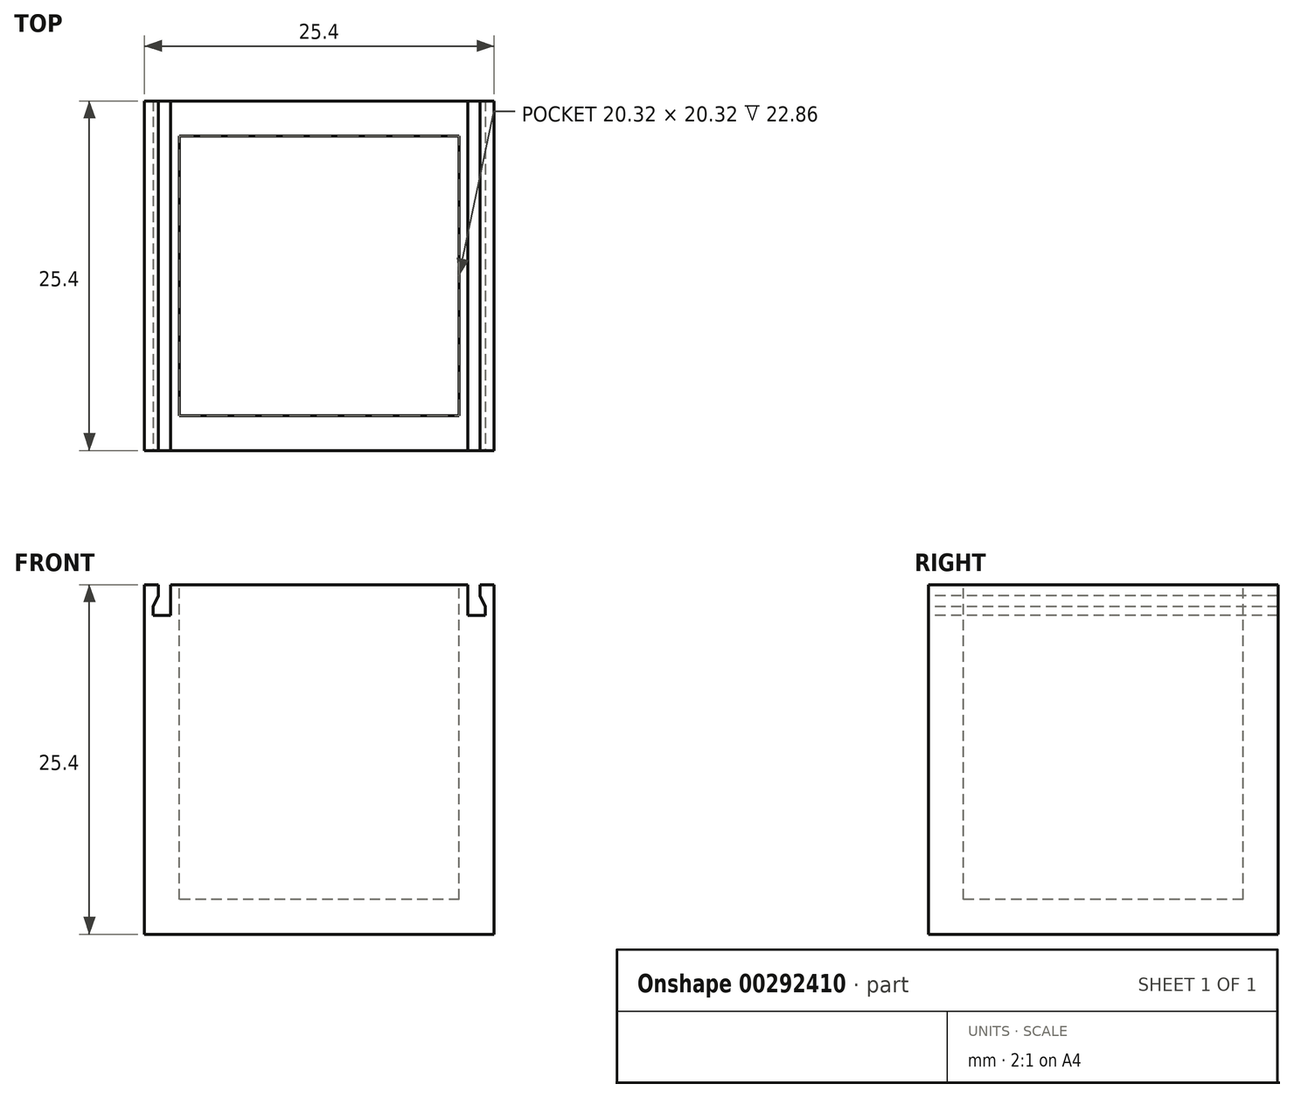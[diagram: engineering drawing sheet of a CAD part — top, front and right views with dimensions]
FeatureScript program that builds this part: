
annotation { "Feature Type Name" : "Feature", "Feature Type Description" : "" }
export const myFeature = defineFeature(function(context is Context, id is Id, definition is map)
    precondition{}
    {
        {
            var Q0;
            Q0=qCreatedBy(makeId("Front.planeOp"),FACE);
            var sketch = newSketch(context, id + "F0", { "sketchPlane" : qUnion([Q0])});
            skLineSegment(sketch, "E0.bottom", {"start": v(12.7, -12.7) * mm, "end": v(-12.7, -12.7) * mm});
            skLineSegment(sketch, "E0.top", {"start": v(12.7, 12.7) * mm, "end": v(-12.7, 12.7) * mm});
            skLineSegment(sketch, "E0.left", {"start": v(12.7, -12.7) * mm, "end": v(12.7, 12.7) * mm});
            skLineSegment(sketch, "E0.right", {"start": v(-12.7, -12.7) * mm, "end": v(-12.7, 12.7) * mm});
            skPoint(sketch, "E0.middle", {"position": v(0, 0) * mm});
            skLineSegment(sketch, "E1", {"start": v(0, 0) * mm, "end": v(0, 12.7) * mm});
            skLineSegment(sketch, "E2", {"start": v(-12.7, 12.7) * mm, "end": v(0, 12.7) * mm});
            skSolve(sketch);
        }
        {
            var Q0;
            Q0=qCreatedBy(makeId("Top.planeOp"),FACE);
            var sketch = newSketch(context, id + "F1", { "sketchPlane" : qUnion([Q0])});
            skLineSegment(sketch, "E3", {"start": v(0, 0) * mm, "end": v(0, 12.7) * mm});
            skLineSegment(sketch, "E4.bottom", {"start": v(11.43, 1.27) * mm, "end": v(-11.43, 1.27) * mm});
            skLineSegment(sketch, "E4.top", {"start": v(11.43, 24.13) * mm, "end": v(-11.43, 24.13) * mm});
            skLineSegment(sketch, "E4.left", {"start": v(11.43, 1.27) * mm, "end": v(11.43, 24.13) * mm});
            skLineSegment(sketch, "E4.right", {"start": v(-11.43, 1.27) * mm, "end": v(-11.43, 24.13) * mm});
            skPoint(sketch, "E4.middle", {"position": v(0, 12.7) * mm});
            skSolve(sketch);
        }
        {
            var Q0;
            Q0=makeQuery(id+"F1.imprint","IMPRINT",FACE,{"disambiguationData":[TD([[makeQuery(id+"F1.imprint","IMPRINT",EDGE,{"derivedFrom":sQuery(id+"F1.wireOp",EDGE,"E4.top")}),1.0]])]});
            extrude(context, id + "F2", {"entities" : qUnion([Q0]), "endBound" : BoundingType.SYMMETRIC, "depth" : 22.86 * mm});
        }
        {
            var Q0;
            Q0 = qSketchRegion(id + "F0", true);
            extrude(context, id + "F3", {"entities" : qUnion([Q0]), "oppositeDirection" : true, "depth" : 25.4 * mm});
        }
        {
            var Q0;
            Q0=makeQuery(id+"F3.opExtrude","SWEPT_FACE",FACE,{"disambiguationData":[OSD([sQuery(id+"F0.wireOp",EDGE,"E0.top"),sQuery(id+"F0.wireOp",EDGE,"E2")])]});
            shell(context, id + "F4", {"entities" : qUnion([Q0]), "thickness" : 2.54 * mm});
        }
        {
            var Q0;
            Q0=makeQuery(id+"F2.opExtrude","SWEPT_BODY",BODY,{"disambiguationData":[OSD([sQuery(id+"F1.wireOp",EDGE,"E4.bottom"),sQuery(id+"F1.wireOp",EDGE,"E4.top"),sQuery(id+"F1.wireOp",EDGE,"E4.left"),sQuery(id+"F1.wireOp",EDGE,"E4.right")])]});
            deleteBodies(context, id + "F5", {"entities" : qUnion([Q0])});
        }
        {
            var Q0;
            Q0=qCreatedBy(makeId("Front.planeOp"),FACE);
            var sketch = newSketch(context, id + "F6", { "sketchPlane" : qUnion([Q0])});
            skLineSegment(sketch, "E5.bottom", {"start": v(-10.8, 10.48) * mm, "end": v(-12.06, 10.48) * mm});
            skLineSegment(sketch, "E5.left", {"start": v(-10.8, 10.48) * mm, "end": v(-10.8, 11.11) * mm});
            skLineSegment(sketch, "E5.right", {"start": v(-12.06, 10.48) * mm, "end": v(-12.06, 11.11) * mm});
            skLineSegment(sketch, "E6.bottom", {"start": v(12.07, 10.48) * mm, "end": v(10.8, 10.48) * mm});
            skLineSegment(sketch, "E6.left", {"start": v(12.07, 10.48) * mm, "end": v(12.07, 11.11) * mm});
            skLineSegment(sketch, "E6.right", {"start": v(10.8, 10.48) * mm, "end": v(10.8, 11.11) * mm});
            skLineSegment(sketch, "E7.0", {"start": v(-11.68, 12.7) * mm, "end": v(-11.68, 11.9) * mm});
            skLineSegment(sketch, "E8.0", {"start": v(11.68, 12.7) * mm, "end": v(11.68, 11.9) * mm});
            skLineSegment(sketch, "E9", {"start": v(11.68, 11.9) * mm, "end": v(12.07, 11.11) * mm});
            skLineSegment(sketch, "E10", {"start": v(-12.06, 11.11) * mm, "end": v(-11.68, 11.9) * mm});
            skLineSegment(sketch, "E11", {"start": v(-10.8, 11.11) * mm, "end": v(-10.8, 12.7) * mm});
            skLineSegment(sketch, "E12", {"start": v(-11.68, 12.7) * mm, "end": v(-10.8, 12.7) * mm});
            skLineSegment(sketch, "E13", {"start": v(10.8, 11.11) * mm, "end": v(10.8, 12.7) * mm});
            skLineSegment(sketch, "E14", {"start": v(10.8, 12.7) * mm, "end": v(11.68, 12.7) * mm});
            skSolve(sketch);
        }
        {
            var Q0;
            Q0=makeQuery(id+"F6.imprint","IMPRINT",FACE,{"disambiguationData":[TD([[makeQuery(id+"F6.imprint","IMPRINT",EDGE,{"derivedFrom":sQuery(id+"F6.wireOp",EDGE,"E5.bottom")}),-1.0]])]});
            var Q1;
            Q1=makeQuery(id+"F6.imprint","IMPRINT",FACE,{"disambiguationData":[TD([[makeQuery(id+"F6.imprint","IMPRINT",EDGE,{"derivedFrom":sQuery(id+"F6.wireOp",EDGE,"E6.bottom")}),-1.0]])]});
            extrude(context, id + "F7", {"entities" : qUnion([Q0, Q1]), "operationType" : NewBodyOperationType.REMOVE, "oppositeDirection" : true, "depth" : 25.4 * mm});
        }
    });
